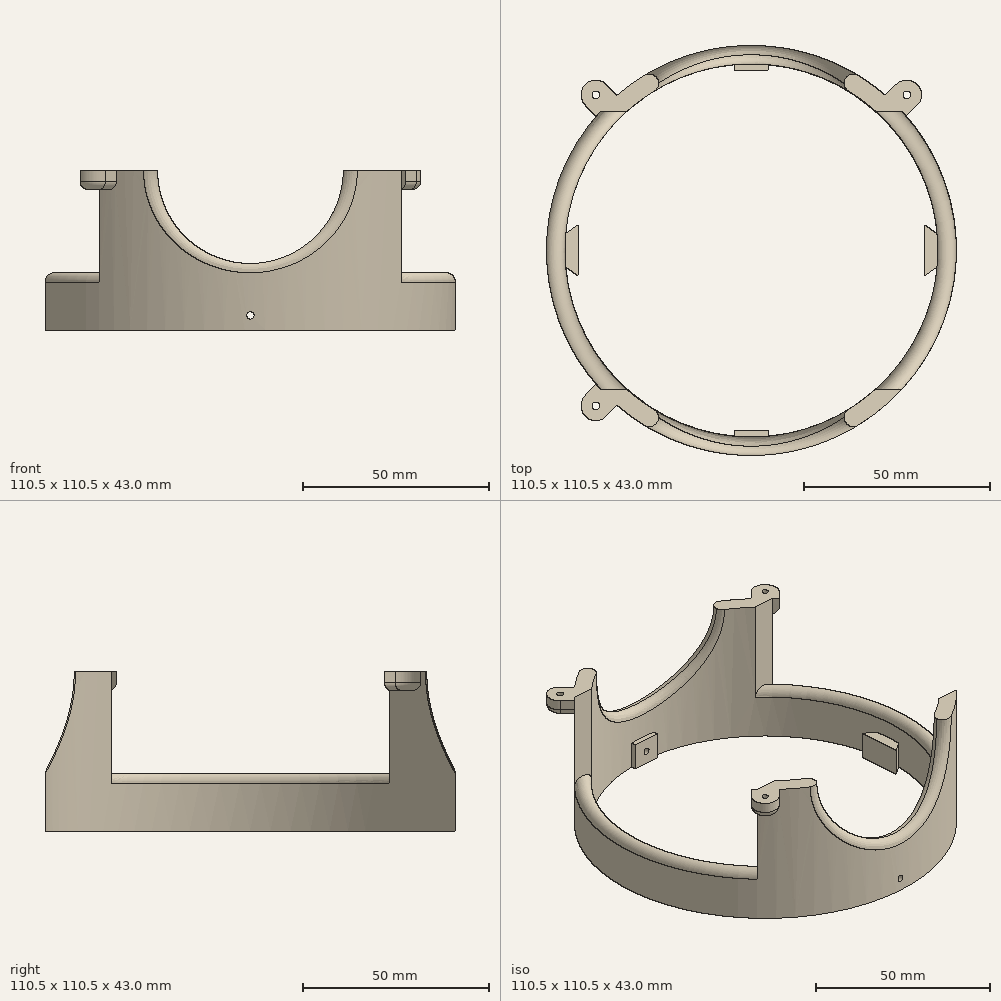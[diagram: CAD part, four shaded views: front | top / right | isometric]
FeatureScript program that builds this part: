
annotation { "Feature Type Name" : "Feature", "Feature Type Description" : "" }
export const myFeature = defineFeature(function(context is Context, id is Id, definition is map)
    precondition{}
    {
        {
            var Q0;
            Q0=qCreatedBy(makeId("Top.planeOp"),FACE);
            var sketch = newSketch(context, id + "F0", { "sketchPlane" : qUnion([Q0])});
            skArc(sketch, "E0", {"start": v(-50.05, -4.5) * mm, "mid": v(-35.53, -35.53) * mm, "end": v(-4.5, -50.05) * mm});
            skCircle(sketch, "E1", {"center": v(0, 0) * mm, "radius": 55.25 * mm});
            skLineSegment(sketch, "E2.2.0.2", {"start": v(4.5, 50.05) * mm, "end": v(4.5, 48.55) * mm});
            skLineSegment(sketch, "E2.2.0.3", {"start": v(-4.5, 50.05) * mm, "end": v(-4.5, 48.55) * mm});
            skArc(sketch, "E3.trimOffspring", {"start": v(50.05, 4.5) * mm, "mid": v(35.53, 35.53) * mm, "end": v(4.5, 50.05) * mm});
            skArc(sketch, "E4.trimOffspring", {"start": v(4.5, -50.05) * mm, "mid": v(35.53, -35.53) * mm, "end": v(50.05, -4.5) * mm});
            skArc(sketch, "E5.trimOffspring", {"start": v(-4.5, 50.05) * mm, "mid": v(-35.53, 35.53) * mm, "end": v(-50.05, 4.5) * mm});
            skLineSegment(sketch, "E6", {"start": v(-46.55, 7) * mm, "end": v(-46.55, -7) * mm});
            skLineSegment(sketch, "E7", {"start": v(-50.05, 4.5) * mm, "end": v(-46.55, 7) * mm});
            skLineSegment(sketch, "E8", {"start": v(-50.05, -4.5) * mm, "end": v(-46.55, -7) * mm});
            skLineSegment(sketch, "E9.MirrorCS", {"start": v(50.05, -4.5) * mm, "end": v(46.55, -7) * mm});
            skLineSegment(sketch, "E10.MirrorCS", {"start": v(50.05, 4.5) * mm, "end": v(46.55, 7) * mm});
            skLineSegment(sketch, "E11.MirrorCS", {"start": v(46.55, 7) * mm, "end": v(46.55, -7) * mm});
            skLineSegment(sketch, "E12", {"start": v(-4.5, 48.55) * mm, "end": v(4.5, 48.55) * mm});
            skLineSegment(sketch, "E13.MirrorCS", {"start": v(-4.5, -50.05) * mm, "end": v(-4.5, -48.55) * mm});
            skLineSegment(sketch, "E14.MirrorCS", {"start": v(4.5, -50.05) * mm, "end": v(4.5, -48.55) * mm});
            skLineSegment(sketch, "E15.MirrorCS", {"start": v(-4.5, -48.55) * mm, "end": v(4.5, -48.55) * mm});
            skSolve(sketch);
        }
        {
            var Q0;
            Q0=qSketchRegion(id+"F0",true);
            extrude(context, id + "F1", {"entities" : qUnion([Q0]), "depth" : 43 * mm});
        }
        {
            var Q0;
            Q0=qCreatedBy(makeId("Front.planeOp"),FACE);
            var sketch = newSketch(context, id + "F2", { "sketchPlane" : qUnion([Q0])});
            skCircle(sketch, "E16", {"center": v(0, 43) * mm, "radius": 25 * mm});
            skLineSegment(sketch, "E17", {"start": v(0, 0) * mm, "end": v(0, 43) * mm});
            skSolve(sketch);
        }
        {
            var Q0;
            Q0=qSketchRegion(id+"F2",true);
            extrude(context, id + "F3", {"entities" : qUnion([Q0]), "operationType" : NewBodyOperationType.REMOVE, "endBound" : BoundingType.SYMMETRIC, "oppositeDirection" : true, "depth" : 162.8 * mm});
        }
        {
            var Q0;
            Q0=makeQuery(id+"F1.opExtrude","CAP_FACE",FACE,{"disambiguationData":[OSD([sQuery(id+"F0.wireOp",EDGE,"E0"),sQuery(id+"F0.wireOp",EDGE,"E1"),sQuery(id+"F0.wireOp",EDGE,"KXo9hoNV-a9ZN-jEZJ-Yrdq-8QQVipn73RV8.bottom"),sQuery(id+"F0.wireOp",EDGE,"KXo9hoNV-a9ZN-jEZJ-Yrdq-8QQVipn73RV8.top"),sQuery(id+"F0.wireOp",EDGE,"KXo9hoNV-a9ZN-jEZJ-Yrdq-8QQVipn73RV8.right"),sQuery(id+"F0.wireOp",EDGE,"E2.1.0.1"),sQuery(id+"F0.wireOp",EDGE,"E2.1.0.2"),sQuery(id+"F0.wireOp",EDGE,"E2.1.0.3"),sQuery(id+"F0.wireOp",EDGE,"E2.2.0.0"),sQuery(id+"F0.wireOp",EDGE,"E2.2.0.2"),sQuery(id+"F0.wireOp",EDGE,"E2.2.0.3"),sQuery(id+"F0.wireOp",EDGE,"E2.3.0.1"),sQuery(id+"F0.wireOp",EDGE,"E2.3.0.2"),sQuery(id+"F0.wireOp",EDGE,"E2.3.0.3"),sQuery(id+"F0.wireOp",EDGE,"E3.trimOffspring"),sQuery(id+"F0.wireOp",EDGE,"E4.trimOffspring"),sQuery(id+"F0.wireOp",EDGE,"E5.trimOffspring")])],"isStart":false});
            var sketch = newSketch(context, id + "F4", { "sketchPlane" : qUnion([Q0])});
            skLineSegment(sketch, "E18", {"start": v(-55.25, 0) * mm, "end": v(55.25, 0) * mm, "construction": true});
            skPoint(sketch, "E19.orphan", {"position": v(42.3, -27.11) * mm});
            skPoint(sketch, "E20.orphan", {"position": v(-42.3, -27.11) * mm});
            skLineSegment(sketch, "E21", {"start": v(39.07, -39.07) * mm, "end": v(0, 0) * mm, "construction": true});
            skLineSegment(sketch, "E22", {"start": v(-39.07, -39.07) * mm, "end": v(0, 0) * mm, "construction": true});
            skLineSegment(sketch, "E23", {"start": v(-39.07, 39.07) * mm, "end": v(0, 0) * mm, "construction": true});
            skLineSegment(sketch, "E24", {"start": v(39.07, 39.07) * mm, "end": v(0, 0) * mm, "construction": true});
            skArc(sketch, "E25", {"start": v(-39.07, 44.72) * mm, "mid": v(-44.72, 44.72) * mm, "end": v(-44.72, 39.07) * mm});
            skArc(sketch, "E26", {"start": v(44.72, 39.07) * mm, "mid": v(44.72, 44.72) * mm, "end": v(39.07, 44.72) * mm});
            skArc(sketch, "E27", {"start": v(-44.72, -39.07) * mm, "mid": v(-44.72, -44.72) * mm, "end": v(-39.07, -44.72) * mm});
            skArc(sketch, "E28", {"start": v(39.07, -44.72) * mm, "mid": v(44.72, -44.72) * mm, "end": v(44.72, -39.07) * mm});
            skLineSegment(sketch, "E29", {"start": v(-44.72, 39.07) * mm, "end": v(-41.8, 36.14) * mm});
            skLineSegment(sketch, "E30", {"start": v(-39.07, 44.72) * mm, "end": v(-36.14, 41.8) * mm});
            skLineSegment(sketch, "E31", {"start": v(39.07, 44.72) * mm, "end": v(36.14, 41.8) * mm});
            skLineSegment(sketch, "E32", {"start": v(44.72, 39.07) * mm, "end": v(41.8, 36.14) * mm});
            skLineSegment(sketch, "E33", {"start": v(-39.07, -44.72) * mm, "end": v(-36.14, -41.8) * mm});
            skLineSegment(sketch, "E34", {"start": v(-44.72, -39.07) * mm, "end": v(-41.8, -36.14) * mm});
            skLineSegment(sketch, "E35", {"start": v(39.07, -44.72) * mm, "end": v(36.14, -41.8) * mm});
            skLineSegment(sketch, "E36", {"start": v(44.72, -39.07) * mm, "end": v(41.8, -36.14) * mm});
            skCircle(sketch, "E37", {"center": v(41.9, -41.9) * mm, "radius": 1 * mm});
            skCircle(sketch, "E38", {"center": v(-41.9, -41.9) * mm, "radius": 1 * mm});
            skCircle(sketch, "E39", {"center": v(41.9, 41.9) * mm, "radius": 1 * mm});
            skCircle(sketch, "E40", {"center": v(-41.9, 41.9) * mm, "radius": 1 * mm});
            skArc(sketch, "E41", {"start": v(50.25, 0) * mm, "mid": v(0, 50.25) * mm, "end": v(-50.25, 0) * mm});
            skLineSegment(sketch, "E42", {"start": v(-55.25, 0) * mm, "end": v(55.25, 0) * mm});
            skArc(sketch, "E43", {"start": v(55.25, 0) * mm, "mid": v(0, 55.25) * mm, "end": v(-55.25, 0) * mm});
            skSolve(sketch);
        }
        {
            var Q0;
            Q0=qSketchRegion(id+"F2",true);
            extrude(context, id + "F5", {"entities" : qUnion([Q0]), "operationType" : NewBodyOperationType.REMOVE, "endBound" : BoundingType.SYMMETRIC, "oppositeDirection" : true, "depth" : 172.6 * mm});
        }
        {
            var Q0;
            Q0=qCreatedBy(makeId("Right.planeOp"),FACE);
            var sketch = newSketch(context, id + "F6", { "sketchPlane" : qUnion([Q0])});
            skLineSegment(sketch, "E44.bottom", {"start": v(-37.5, 115.5) * mm, "end": v(37.5, 115.5) * mm});
            skLineSegment(sketch, "E44.top", {"start": v(-37.5, 15.5) * mm, "end": v(37.5, 15.5) * mm});
            skLineSegment(sketch, "E44.left", {"start": v(-37.5, 115.5) * mm, "end": v(-37.5, 15.5) * mm});
            skLineSegment(sketch, "E44.right", {"start": v(37.5, 115.5) * mm, "end": v(37.5, 15.5) * mm});
            skLineSegment(sketch, "E45", {"start": v(0, 0) * mm, "end": v(0, 15.5) * mm, "construction": true});
            skSolve(sketch);
        }
        {
            var Q0;
            Q0=qSketchRegion(id+"F6",true);
            extrude(context, id + "F7", {"entities" : qUnion([Q0]), "operationType" : NewBodyOperationType.REMOVE, "endBound" : BoundingType.SYMMETRIC, "depth" : 182.4 * mm});
        }
        {
            var Q0;
            Q0=makeQuery(id+"F4.imprint","IMPRINT",FACE,{"disambiguationData":[TD([[makeQuery(id+"F4.imprint","IMPRINT",EDGE,{"derivedFrom":sQuery(id+"F4.wireOp",EDGE,"E28")}),1.0]])]});
            var Q1;
            Q1=makeQuery(id+"F4.imprint","IMPRINT",FACE,{"disambiguationData":[TD([[makeQuery(id+"F4.imprint","IMPRINT",EDGE,{"derivedFrom":sQuery(id+"F4.wireOp",EDGE,"E27")}),1.0]])]});
            var Q2;
            Q2=makeQuery(id+"F4.imprint","IMPRINT",FACE,{"disambiguationData":[TD([[makeQuery(id+"F4.imprint","IMPRINT",EDGE,{"derivedFrom":sQuery(id+"F4.wireOp",EDGE,"E25")}),1.0]])]});
            var Q3;
            Q3=makeQuery(id+"F4.imprint","IMPRINT",FACE,{"disambiguationData":[TD([[makeQuery(id+"F4.imprint","IMPRINT",EDGE,{"derivedFrom":sQuery(id+"F4.wireOp",EDGE,"E26")}),1.0]])]});
            extrude(context, id + "F8", {"entities" : qUnion([Q0, Q1, Q2, Q3]), "operationType" : NewBodyOperationType.ADD, "oppositeDirection" : true, "depth" : 5 * mm});
        }
        {
            var Q0;
            Q0=makeQuery(id+"F8.opExtrude","CAP_EDGE",EDGE,{"disambiguationData":[OSD([sQuery(id+"F4.wireOp",EDGE,"E26")])],"isStart":false});
            var Q1;
            Q1=makeQuery(id+"F8.opExtrude","CAP_EDGE",EDGE,{"disambiguationData":[OSD([sQuery(id+"F4.wireOp",EDGE,"E28")])],"isStart":false});
            var Q2;
            Q2=makeQuery(id+"F8.opExtrude","CAP_EDGE",EDGE,{"disambiguationData":[OSD([sQuery(id+"F4.wireOp",EDGE,"E27")])],"isStart":false});
            var Q3;
            Q3=makeQuery(id+"F8.opExtrude","CAP_EDGE",EDGE,{"disambiguationData":[OSD([sQuery(id+"F4.wireOp",EDGE,"E25")])],"isStart":false});
            fillet(context, id + "F9", {"entities" : qUnion([Q0, Q1, Q2, Q3]), "radius" : 2 * mm, "tangentPropagation" : true, "allowEdgeOverflow" : false});
        }
        {
            var Q0;
            Q0=makeQuery(id+"F1.opExtrude","SWEPT_FACE",FACE,{"disambiguationData":[OSD([sQuery(id+"F0.wireOp",EDGE,"E15.MirrorCS")])]});
            var sketch = newSketch(context, id + "F10", { "sketchPlane" : qUnion([Q0])});
            skCircle(sketch, "E46", {"center": v(0, 4) * mm, "radius": 0.82 * mm});
            skSolve(sketch);
        }
        {
            var Q0;
            Q0=sQuery(id+"F10.wireOp",VERTEX,"E46.center");
            var Q1;
            Q1=makeQuery(id+"F1.opExtrude","SWEPT_BODY",BODY,{"disambiguationData":[OSD([sQuery(id+"F0.wireOp",EDGE,"E0"),sQuery(id+"F0.wireOp",EDGE,"E1"),sQuery(id+"F0.wireOp",EDGE,"E2.2.0.0"),sQuery(id+"F0.wireOp",EDGE,"E2.2.0.2"),sQuery(id+"F0.wireOp",EDGE,"E2.2.0.3"),sQuery(id+"F0.wireOp",EDGE,"E2.3.0.1"),sQuery(id+"F0.wireOp",EDGE,"E2.3.0.2"),sQuery(id+"F0.wireOp",EDGE,"E2.3.0.3"),sQuery(id+"F0.wireOp",EDGE,"E3.trimOffspring"),sQuery(id+"F0.wireOp",EDGE,"E4.trimOffspring"),sQuery(id+"F0.wireOp",EDGE,"E5.trimOffspring"),sQuery(id+"F0.wireOp",EDGE,"0wMoWTtO-hKPG-dmUJ-9eZK-Rki3Ka56Pj0p"),sQuery(id+"F0.wireOp",EDGE,"V7nILoa6-agM4-B80q-80k6-MabAC6LeFQ3d"),sQuery(id+"F0.wireOp",EDGE,"T4tWseir-YMXC-WR8s-1T1N-fBKYRdHiWXzI"),sQuery(id+"F0.wireOp",EDGE,"GhSFunWE-UcgT-IK5w-9III-MmuMwgvZ9d2i"),sQuery(id+"F0.wireOp",EDGE,"6XujKZao-lyGk-p0ZG-WLlf-O7pdLShlOZ0q"),sQuery(id+"F0.wireOp",EDGE,"wTnajsCB-XfUZ-x2k5-9YjB-GDWOXe4ybcG3")])]});
            hole(context, id + "F11", {"style" : HoleStyle.SIMPLE, "endStyle" : HoleEndStyle.THROUGH, "holeDiameter" : 2 * mm, "isTappedThrough" : true, "tappedDepth" : 12 * mm, "tapClearance" : 3, "startFromSketch" : true, "locations" : qUnion([Q0]), "scope" : qUnion([Q1])});
        }
        {
            var Q0;
            Q0=makeQuery(id+"F1.opExtrude","SWEPT_FACE",FACE,{"disambiguationData":[OSD([sQuery(id+"F0.wireOp",EDGE,"E12")])]});
            var sketch = newSketch(context, id + "F12", { "sketchPlane" : qUnion([Q0])});
            skCircle(sketch, "E47", {"center": v(0, 4) * mm, "radius": 0.9 * mm});
            skSolve(sketch);
        }
        {
            var Q0;
            Q0=sQuery(id+"F12.wireOp",VERTEX,"E47.center");
            var Q1;
            Q1=makeQuery(id+"F1.opExtrude","SWEPT_BODY",BODY,{"disambiguationData":[OSD([sQuery(id+"F0.wireOp",EDGE,"E0"),sQuery(id+"F0.wireOp",EDGE,"E1"),sQuery(id+"F0.wireOp",EDGE,"E2.2.0.0"),sQuery(id+"F0.wireOp",EDGE,"E2.2.0.2"),sQuery(id+"F0.wireOp",EDGE,"E2.2.0.3"),sQuery(id+"F0.wireOp",EDGE,"E2.3.0.1"),sQuery(id+"F0.wireOp",EDGE,"E2.3.0.2"),sQuery(id+"F0.wireOp",EDGE,"E2.3.0.3"),sQuery(id+"F0.wireOp",EDGE,"E3.trimOffspring"),sQuery(id+"F0.wireOp",EDGE,"E4.trimOffspring"),sQuery(id+"F0.wireOp",EDGE,"E5.trimOffspring"),sQuery(id+"F0.wireOp",EDGE,"0wMoWTtO-hKPG-dmUJ-9eZK-Rki3Ka56Pj0p"),sQuery(id+"F0.wireOp",EDGE,"V7nILoa6-agM4-B80q-80k6-MabAC6LeFQ3d"),sQuery(id+"F0.wireOp",EDGE,"T4tWseir-YMXC-WR8s-1T1N-fBKYRdHiWXzI"),sQuery(id+"F0.wireOp",EDGE,"GhSFunWE-UcgT-IK5w-9III-MmuMwgvZ9d2i"),sQuery(id+"F0.wireOp",EDGE,"6XujKZao-lyGk-p0ZG-WLlf-O7pdLShlOZ0q"),sQuery(id+"F0.wireOp",EDGE,"wTnajsCB-XfUZ-x2k5-9YjB-GDWOXe4ybcG3")])]});
            hole(context, id + "F13", {"style" : HoleStyle.SIMPLE, "endStyle" : HoleEndStyle.THROUGH, "holeDiameter" : 2 * mm, "isTappedThrough" : true, "tappedDepth" : 12 * mm, "tapClearance" : 3, "startFromSketch" : true, "locations" : qUnion([Q0]), "scope" : qUnion([Q1])});
        }
        {
            var Q0;
            Q0=makeQuery(id+"F1.opExtrude","CAP_FACE",FACE,{"disambiguationData":[OSD([sQuery(id+"F0.wireOp",EDGE,"E0"),sQuery(id+"F0.wireOp",EDGE,"E1"),sQuery(id+"F0.wireOp",EDGE,"E2.2.0.0"),sQuery(id+"F0.wireOp",EDGE,"E2.2.0.2"),sQuery(id+"F0.wireOp",EDGE,"E2.2.0.3"),sQuery(id+"F0.wireOp",EDGE,"E2.3.0.1"),sQuery(id+"F0.wireOp",EDGE,"E2.3.0.2"),sQuery(id+"F0.wireOp",EDGE,"E2.3.0.3"),sQuery(id+"F0.wireOp",EDGE,"E3.trimOffspring"),sQuery(id+"F0.wireOp",EDGE,"E4.trimOffspring"),sQuery(id+"F0.wireOp",EDGE,"E5.trimOffspring"),sQuery(id+"F0.wireOp",EDGE,"0wMoWTtO-hKPG-dmUJ-9eZK-Rki3Ka56Pj0p"),sQuery(id+"F0.wireOp",EDGE,"V7nILoa6-agM4-B80q-80k6-MabAC6LeFQ3d"),sQuery(id+"F0.wireOp",EDGE,"T4tWseir-YMXC-WR8s-1T1N-fBKYRdHiWXzI"),sQuery(id+"F0.wireOp",EDGE,"GhSFunWE-UcgT-IK5w-9III-MmuMwgvZ9d2i"),sQuery(id+"F0.wireOp",EDGE,"6XujKZao-lyGk-p0ZG-WLlf-O7pdLShlOZ0q"),sQuery(id+"F0.wireOp",EDGE,"wTnajsCB-XfUZ-x2k5-9YjB-GDWOXe4ybcG3")])],"isStart":true});
            cPlane(context, id + "F14", {"entities" : qUnion([Q0]), "cplaneType" : CPlaneType.OFFSET, "offset" : 8 * mm, "oppositeDirection" : true, "width" : 150 * mm, "height" : 150 * mm});
        }
        {
            var Q0;
            Q0=qCreatedBy(id+"F14.planeOp",FACE);
            var sketch = newSketch(context, id + "F15", { "sketchPlane" : qUnion([Q0])});
            skCircle(sketch, "E48", {"center": v(0, 0) * mm, "radius": 50.25 * mm});
            skSolve(sketch);
        }
        {
            var Q0;
            Q0=qSketchRegion(id+"F15",true);
            var Q1;
            Q1=sQuery(id+"F15.wireOp",EDGE,"E48");
            extrude(context, id + "F16", {"entities" : qUnion([Q0]), "operationType" : NewBodyOperationType.REMOVE, "surfaceEntities" : qUnion([Q1]), "oppositeDirection" : true, "depth" : 73.1 * mm});
        }
        {
            var Q0;
            Q0=makeQuery(id+"F7.boolean.opBoolean","INTERSECT",EDGE,{"disambiguationData":[OD(0.0)],"derivedFrom":[makeQuery(id+"F1.opExtrude","SWEPT_FACE",FACE,{"disambiguationData":[OSD([sQuery(id+"F0.wireOp",EDGE,"E1")])]}),makeQuery(id+"F7.opExtrude","SWEPT_FACE",FACE,{"disambiguationData":[OSD([sQuery(id+"F6.wireOp",EDGE,"E44.top")])]})]});
            var Q1;
            {var subQ0=makeQuery(id+"F7.opExtrude","SWEPT_FACE",FACE,{"disambiguationData":[OSD([sQuery(id+"F6.wireOp",EDGE,"E44.top")])]});Q1=makeQuery(id+"F16.boolean.opBoolean","MERGE",EDGE,{"derivedFrom":[makeQuery(id+"F7.boolean.opBoolean","INTERSECT",EDGE,{"derivedFrom":[makeQuery(id+"F1.opExtrude","SWEPT_FACE",FACE,{"disambiguationData":[OSD([sQuery(id+"F0.wireOp",EDGE,"E3.trimOffspring")])]}),subQ0]}),makeQuery(id+"F7.boolean.opBoolean","INTERSECT",EDGE,{"derivedFrom":[makeQuery(id+"F1.opExtrude","SWEPT_FACE",FACE,{"disambiguationData":[OSD([sQuery(id+"F0.wireOp",EDGE,"E4.trimOffspring")])]}),subQ0]})]});}
            var Q2;
            Q2=makeQuery(id+"F7.boolean.opBoolean","INTERSECT",EDGE,{"disambiguationData":[OD(1.0)],"derivedFrom":[makeQuery(id+"F1.opExtrude","SWEPT_FACE",FACE,{"disambiguationData":[OSD([sQuery(id+"F0.wireOp",EDGE,"E1")])]}),makeQuery(id+"F7.opExtrude","SWEPT_FACE",FACE,{"disambiguationData":[OSD([sQuery(id+"F6.wireOp",EDGE,"E44.top")])]})]});
            var Q3;
            {var subQ0=makeQuery(id+"F7.opExtrude","SWEPT_FACE",FACE,{"disambiguationData":[OSD([sQuery(id+"F6.wireOp",EDGE,"E44.top")])]});Q3=makeQuery(id+"F16.boolean.opBoolean","MERGE",EDGE,{"derivedFrom":[makeQuery(id+"F7.boolean.opBoolean","INTERSECT",EDGE,{"derivedFrom":[makeQuery(id+"F1.opExtrude","SWEPT_FACE",FACE,{"disambiguationData":[OSD([sQuery(id+"F0.wireOp",EDGE,"E0")])]}),subQ0]}),makeQuery(id+"F7.boolean.opBoolean","INTERSECT",EDGE,{"derivedFrom":[makeQuery(id+"F1.opExtrude","SWEPT_FACE",FACE,{"disambiguationData":[OSD([sQuery(id+"F0.wireOp",EDGE,"E5.trimOffspring")])]}),subQ0]})]});}
            fillet(context, id + "F17", {"entities" : qUnion([Q0, Q1, Q2, Q3]), "radius" : 2.5 * mm, "tangentPropagation" : true, "allowEdgeOverflow" : false});
        }
        {
            var Q0;
            Q0=makeQuery(id+"F3.boolean.opBoolean","INTERSECT",EDGE,{"disambiguationData":[OD(0.0)],"derivedFrom":[makeQuery(id+"F1.opExtrude","SWEPT_FACE",FACE,{"disambiguationData":[OSD([sQuery(id+"F0.wireOp",EDGE,"E1")])]}),makeQuery(id+"F3.opExtrude","SWEPT_FACE",FACE,{"disambiguationData":[OSD([sQuery(id+"F2.wireOp",EDGE,"E16")])]})]});
            var Q1;
            Q1=makeQuery(id+"F3.boolean.opBoolean","INTERSECT",EDGE,{"disambiguationData":[OD(1.0)],"derivedFrom":[makeQuery(id+"F1.opExtrude","SWEPT_FACE",FACE,{"disambiguationData":[OSD([sQuery(id+"F0.wireOp",EDGE,"E1")])]}),makeQuery(id+"F3.opExtrude","SWEPT_FACE",FACE,{"disambiguationData":[OSD([sQuery(id+"F2.wireOp",EDGE,"E16")])]})]});
            var Q2;
            {var subQ0=makeQuery(id+"F3.opExtrude","SWEPT_FACE",FACE,{"disambiguationData":[OSD([sQuery(id+"F2.wireOp",EDGE,"E16")])]});Q2=makeQuery(id+"F16.boolean.opBoolean","MERGE",EDGE,{"derivedFrom":[makeQuery(id+"F3.boolean.opBoolean","INTERSECT",EDGE,{"derivedFrom":[makeQuery(id+"F1.opExtrude","SWEPT_FACE",FACE,{"disambiguationData":[OSD([sQuery(id+"F0.wireOp",EDGE,"E0")])]}),subQ0]}),makeQuery(id+"F3.boolean.opBoolean","INTERSECT",EDGE,{"derivedFrom":[makeQuery(id+"F1.opExtrude","SWEPT_FACE",FACE,{"disambiguationData":[OSD([sQuery(id+"F0.wireOp",EDGE,"E4.trimOffspring")])]}),subQ0]})]});}
            var Q3;
            {var subQ0=makeQuery(id+"F3.opExtrude","SWEPT_FACE",FACE,{"disambiguationData":[OSD([sQuery(id+"F2.wireOp",EDGE,"E16")])]});Q3=makeQuery(id+"F16.boolean.opBoolean","MERGE",EDGE,{"derivedFrom":[makeQuery(id+"F3.boolean.opBoolean","INTERSECT",EDGE,{"derivedFrom":[makeQuery(id+"F1.opExtrude","SWEPT_FACE",FACE,{"disambiguationData":[OSD([sQuery(id+"F0.wireOp",EDGE,"E3.trimOffspring")])]}),subQ0]}),makeQuery(id+"F3.boolean.opBoolean","INTERSECT",EDGE,{"derivedFrom":[makeQuery(id+"F1.opExtrude","SWEPT_FACE",FACE,{"disambiguationData":[OSD([sQuery(id+"F0.wireOp",EDGE,"E5.trimOffspring")])]}),subQ0]})]});}
            fillet(context, id + "F18", {"entities" : qUnion([Q0, Q1, Q2, Q3]), "radius" : 2.5 * mm, "tangentPropagation" : true, "allowEdgeOverflow" : false});
        }
    });
